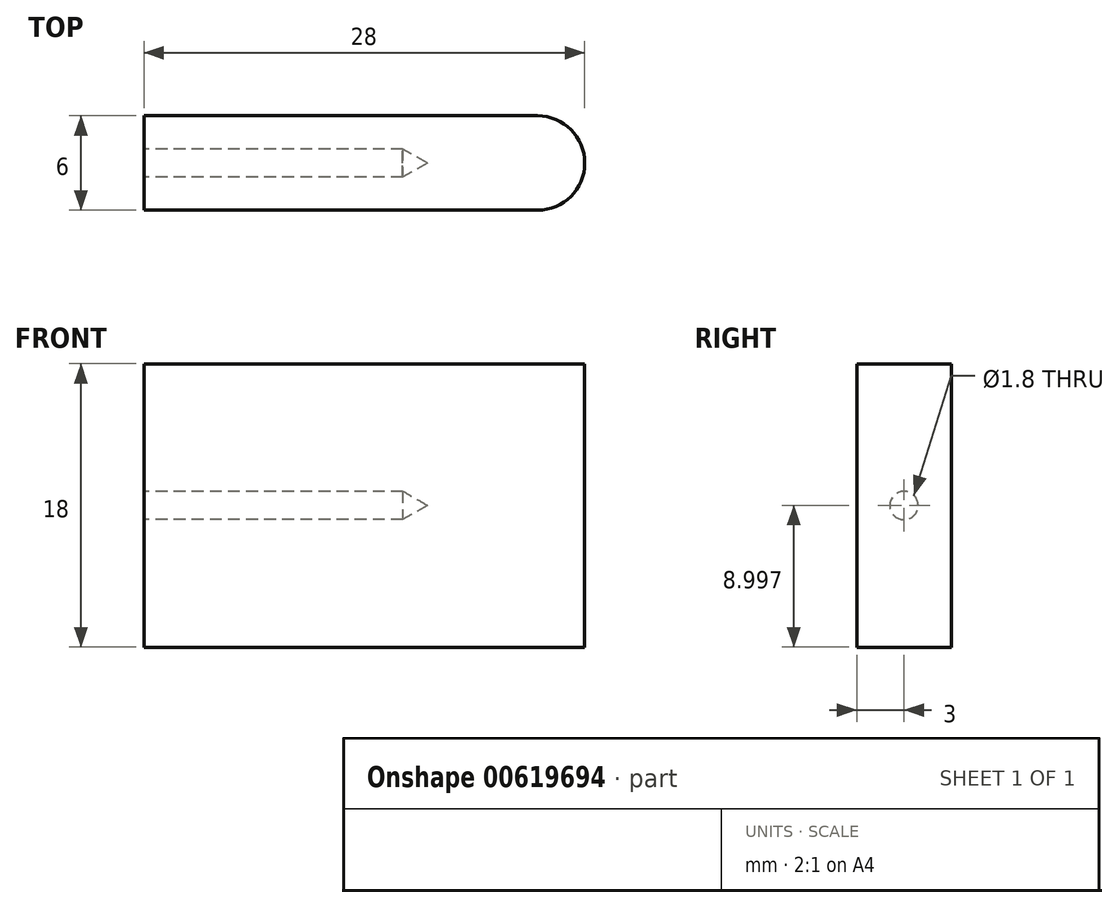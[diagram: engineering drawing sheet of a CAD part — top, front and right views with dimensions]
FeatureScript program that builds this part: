
annotation { "Feature Type Name" : "Feature", "Feature Type Description" : "" }
export const myFeature = defineFeature(function(context is Context, id is Id, definition is map)
    precondition{}
    {
        {
            var Q0;
            Q0=qCreatedBy(makeId("Front.planeOp"),FACE);
            var sketch = newSketch(context, id + "F0", { "sketchPlane" : qUnion([Q0])});
            skLineSegment(sketch, "E0.bottom", {"start": v(-4.57, -4.32) * mm, "end": v(23.43, -4.32) * mm});
            skLineSegment(sketch, "E0.top", {"start": v(-4.57, -22.32) * mm, "end": v(23.43, -22.32) * mm});
            skLineSegment(sketch, "E0.left", {"start": v(-4.57, -4.32) * mm, "end": v(-4.57, -22.32) * mm});
            skLineSegment(sketch, "E0.right", {"start": v(23.43, -4.32) * mm, "end": v(23.43, -22.32) * mm});
            skSolve(sketch);
        }
        {
            var Q0;
            Q0 = qSketchRegion(id + "F0", true);
            extrude(context, id + "F1", {"entities" : qUnion([Q0]), "depth" : 6 * mm, "offsetDistance" : 25 * mm});
        }
        {
            var Q0;
            Q0=makeQuery(id+"F1.opExtrude","SWEPT_FACE",FACE,{"disambiguationData":[OSD([sQuery(id+"F0.wireOp",EDGE,"E0.left")])]});
            var sketch = newSketch(context, id + "F2", { "sketchPlane" : qUnion([Q0])});
            skCircle(sketch, "E1", {"center": v(3, -13.32) * mm, "radius": 0.9 * mm});
            skSolve(sketch);
        }
        {
            var Q0;
            Q0 = qSketchRegion(id + "F2", true);
            extrude(context, id + "F3", {"entities" : qUnion([Q0]), "operationType" : NewBodyOperationType.REMOVE, "oppositeDirection" : true, "depth" : 18 * mm, "offsetDistance" : 25 * mm});
        }
        {
            var Q0;
            Q0=makeQuery(id+"F1.opExtrude","CAP_EDGE",EDGE,{"disambiguationData":[OSD([sQuery(id+"F0.wireOp",EDGE,"E0.right")])],"isStart":false});
            var Q1;
            Q1=makeQuery(id+"F1.opExtrude","CAP_EDGE",EDGE,{"disambiguationData":[OSD([sQuery(id+"F0.wireOp",EDGE,"E0.right")])],"isStart":true});
            fillet(context, id + "F4", {"entities" : qUnion([Q0, Q1]), "radius" : 3 * mm, "tangentPropagation" : true, "allowEdgeOverflow" : false});
        }
        {
            var Q0;
            Q0=makeQuery(id+"F3.boolean.opBoolean","COPY",EDGE,{"derivedFrom":makeQuery(id+"F3.opExtrude","CAP_EDGE",EDGE,{"disambiguationData":[OSD([sQuery(id+"F2.wireOp",EDGE,"E1")])],"isStart":false})});
            chamfer(context, id + "F5", {"entities" : qUnion([Q0]), "chamferType" : ChamferType.OFFSET_ANGLE, "width" : 0.9 * mm, "oppositeDirection" : false, "angle" : 60 * degree, "tangentPropagation" : true});
        }
    });
